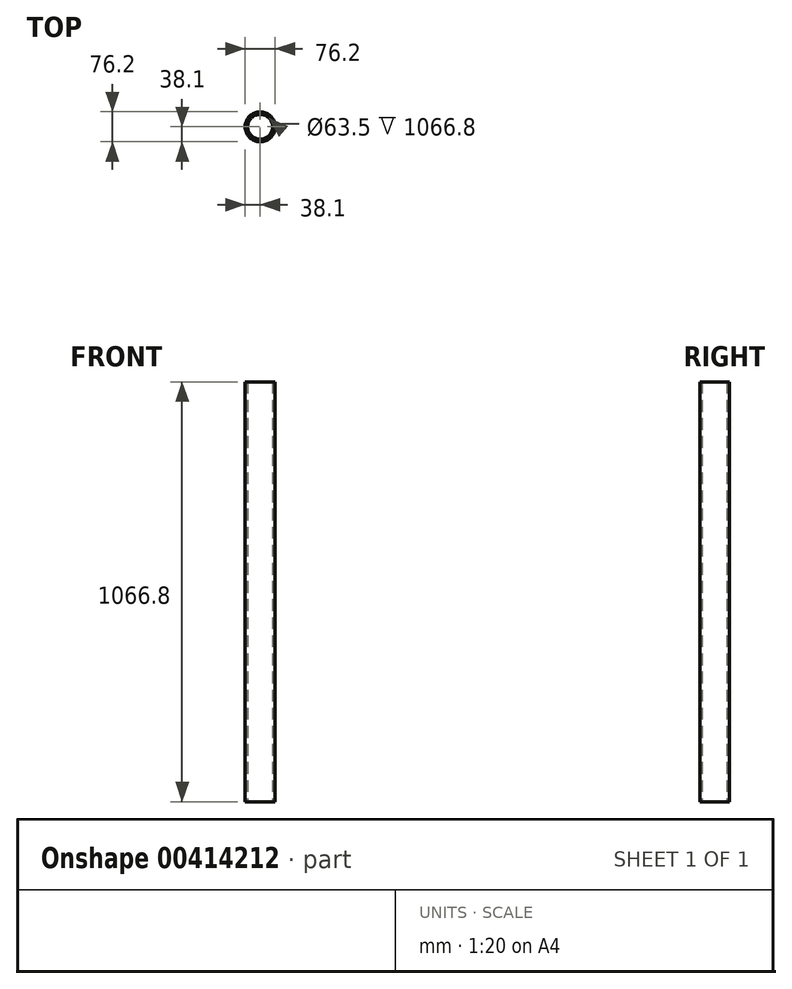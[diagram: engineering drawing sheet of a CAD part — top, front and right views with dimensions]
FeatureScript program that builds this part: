
annotation { "Feature Type Name" : "Feature", "Feature Type Description" : "" }
export const myFeature = defineFeature(function(context is Context, id is Id, definition is map)
    precondition{}
    {
        {
            var Q0;
            Q0=qCreatedBy(makeId("Top.planeOp"),FACE);
            var sketch = newSketch(context, id + "F0", { "sketchPlane" : qUnion([Q0])});
            skCircle(sketch, "E0", {"center": v(0, 0) * mm, "radius": 38.1 * mm});
            skCircle(sketch, "E1", {"center": v(0, 0) * mm, "radius": 31.75 * mm});
            skSolve(sketch);
        }
        {
            var Q0;
            Q0=makeQuery(id+"F0.imprint","IMPRINT",FACE,{"disambiguationData":[TD([[makeQuery(id+"F0.imprint","IMPRINT",EDGE,{"derivedFrom":sQuery(id+"F0.wireOp",EDGE,"E0")}),1.0]])]});
            extrude(context, id + "F1", {"entities" : qUnion([Q0]), "depth" : 1066.8 * mm});
        }
    });
